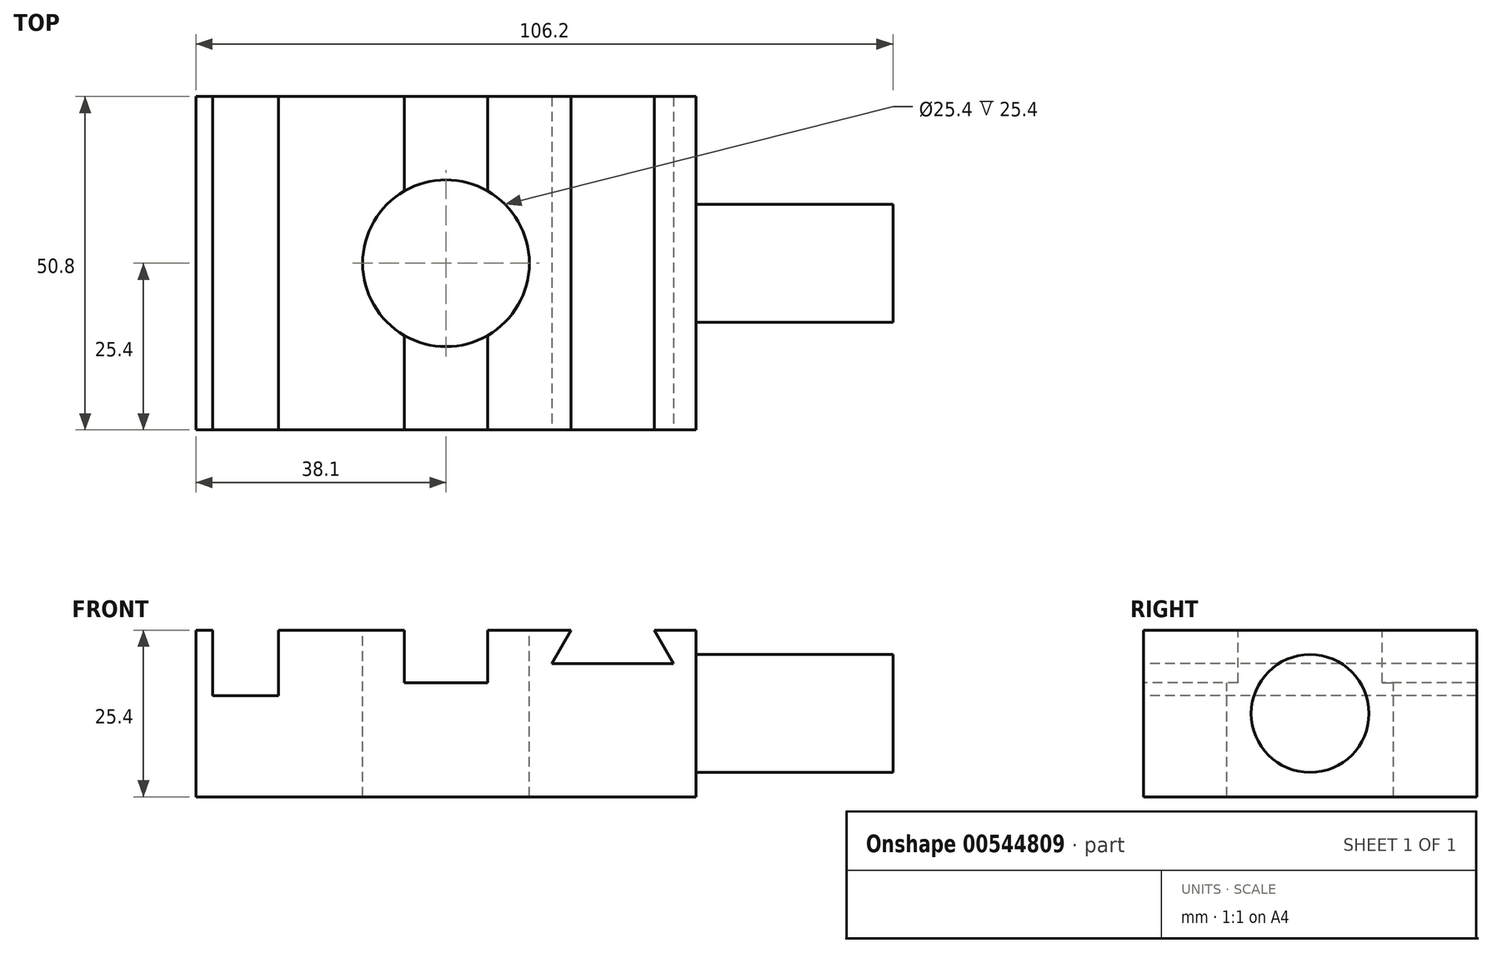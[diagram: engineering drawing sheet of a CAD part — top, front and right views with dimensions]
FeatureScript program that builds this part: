
annotation { "Feature Type Name" : "Feature", "Feature Type Description" : "" }
export const myFeature = defineFeature(function(context is Context, id is Id, definition is map)
    precondition{}
    {
        {
            var Q0;
            Q0=qCreatedBy(makeId("Top.planeOp"),FACE);
            var sketch = newSketch(context, id + "F0", { "sketchPlane" : qUnion([Q0])});
            skLineSegment(sketch, "E0.bottom", {"start": v(38.1, -25.4) * mm, "end": v(-38.1, -25.4) * mm});
            skLineSegment(sketch, "E0.top", {"start": v(38.1, 25.4) * mm, "end": v(-38.1, 25.4) * mm});
            skLineSegment(sketch, "E0.left", {"start": v(38.1, -25.4) * mm, "end": v(38.1, 25.4) * mm});
            skLineSegment(sketch, "E0.right", {"start": v(-38.1, -25.4) * mm, "end": v(-38.1, 25.4) * mm});
            skPoint(sketch, "E0.middle", {"position": v(0, 0) * mm});
            skCircle(sketch, "E1", {"center": v(0, 0) * mm, "radius": 12.7 * mm});
            skSolve(sketch);
        }
        {
            var Q0;
            Q0 = qSketchRegion(id + "F0", true);
            extrude(context, id + "F1", {"entities" : qUnion([Q0]), "oppositeDirection" : true, "depth" : 25.4 * mm, "offsetDistance" : 25 * mm});
        }
        {
            var Q0;
            Q0=qCreatedBy(makeId("Top.planeOp"),FACE);
            var sketch = newSketch(context, id + "F2", { "sketchPlane" : qUnion([Q0])});
            skLineSegment(sketch, "E2.bottom", {"start": v(-35.56, 25.4) * mm, "end": v(-25.56, 25.4) * mm});
            skLineSegment(sketch, "E2.top", {"start": v(-35.56, -25.4) * mm, "end": v(-25.56, -25.4) * mm});
            skLineSegment(sketch, "E2.left", {"start": v(-35.56, 25.4) * mm, "end": v(-35.56, -25.4) * mm});
            skLineSegment(sketch, "E2.right", {"start": v(-25.56, 25.4) * mm, "end": v(-25.56, -25.4) * mm});
            skLineSegment(sketch, "E3.bottom", {"start": v(-6.35, 25.4) * mm, "end": v(6.35, 25.4) * mm});
            skLineSegment(sketch, "E3.top", {"start": v(-6.35, -25.4) * mm, "end": v(6.35, -25.4) * mm});
            skLineSegment(sketch, "E3.left", {"start": v(-6.35, 25.4) * mm, "end": v(-6.35, -25.4) * mm});
            skLineSegment(sketch, "E3.right", {"start": v(6.35, 25.4) * mm, "end": v(6.35, -25.4) * mm});
            skLineSegment(sketch, "E4", {"start": v(0, 25.4) * mm, "end": v(0, -25.4) * mm, "construction": true});
            skSolve(sketch);
        }
        {
            var Q0;
            Q0=makeQuery(id+"F2.imprint","IMPRINT",FACE,{"disambiguationData":[TD([[makeQuery(id+"F2.imprint","IMPRINT",EDGE,{"derivedFrom":sQuery(id+"F2.wireOp",EDGE,"E2.bottom")}),-1.0]])]});
            extrude(context, id + "F3", {"entities" : qUnion([Q0]), "operationType" : NewBodyOperationType.REMOVE, "oppositeDirection" : true, "depth" : 10 * mm, "offsetDistance" : 25 * mm});
        }
        {
            var Q0;
            Q0=makeQuery(id+"F2.imprint","IMPRINT",FACE,{"disambiguationData":[TD([[makeQuery(id+"F2.imprint","IMPRINT",EDGE,{"derivedFrom":sQuery(id+"F2.wireOp",EDGE,"E3.bottom")}),-1.0]])]});
            extrude(context, id + "F4", {"entities" : qUnion([Q0]), "operationType" : NewBodyOperationType.REMOVE, "oppositeDirection" : true, "depth" : 8 * mm, "offsetDistance" : 25 * mm});
        }
        {
            var Q0;
            Q0=makeQuery(id+"F1.opExtrude","SWEPT_FACE",FACE,{"disambiguationData":[OSD([sQuery(id+"F0.wireOp",EDGE,"E0.left")])]});
            var sketch = newSketch(context, id + "F5", { "sketchPlane" : qUnion([Q0])});
            skCircle(sketch, "E5", {"center": v(0, -12.7) * mm, "radius": 8.98 * mm});
            skPoint(sketch, "E5.centerSnap0", {"position": v(-25.4, -12.7) * mm});
            skSolve(sketch);
        }
        {
            var Q0;
            Q0=makeQuery(id+"F5.imprint","IMPRINT",FACE,{"disambiguationData":[TD([[makeQuery(id+"F5.imprint","IMPRINT",EDGE,{"derivedFrom":sQuery(id+"F5.wireOp",EDGE,"E5")}),1.0]])]});
            extrude(context, id + "F6", {"entities" : qUnion([Q0]), "operationType" : NewBodyOperationType.ADD, "depth" : 30 * mm, "offsetDistance" : 25 * mm});
        }
        {
            var Q0;
            Q0=makeQuery(id+"F1.opExtrude","SWEPT_FACE",FACE,{"disambiguationData":[OSD([sQuery(id+"F0.wireOp",EDGE,"E0.bottom")])]});
            var sketch = newSketch(context, id + "F7", { "sketchPlane" : qUnion([Q0])});
            skLineSegment(sketch, "E6", {"start": v(19.05, 0) * mm, "end": v(16.12, -5.08) * mm});
            skLineSegment(sketch, "E7", {"start": v(16.12, -5.08) * mm, "end": v(34.68, -5.08) * mm});
            skLineSegment(sketch, "E8", {"start": v(34.68, -5.08) * mm, "end": v(31.75, 0) * mm});
            skLineSegment(sketch, "E9", {"start": v(31.75, 0) * mm, "end": v(19.05, 0) * mm});
            skLineSegment(sketch, "E10", {"start": v(25.4, -5.08) * mm, "end": v(25.4, 0) * mm, "construction": true});
            skSolve(sketch);
        }
        {
            var Q0;
            Q0=makeQuery(id+"F7.imprint","IMPRINT",FACE,{"disambiguationData":[TD([[makeQuery(id+"F7.imprint","IMPRINT",EDGE,{"derivedFrom":sQuery(id+"F7.wireOp",EDGE,"E6")}),1.0]])]});
            extrude(context, id + "F8", {"entities" : qUnion([Q0]), "operationType" : NewBodyOperationType.REMOVE, "oppositeDirection" : true, "depth" : 50.8 * mm, "offsetDistance" : 25 * mm});
        }
    });
